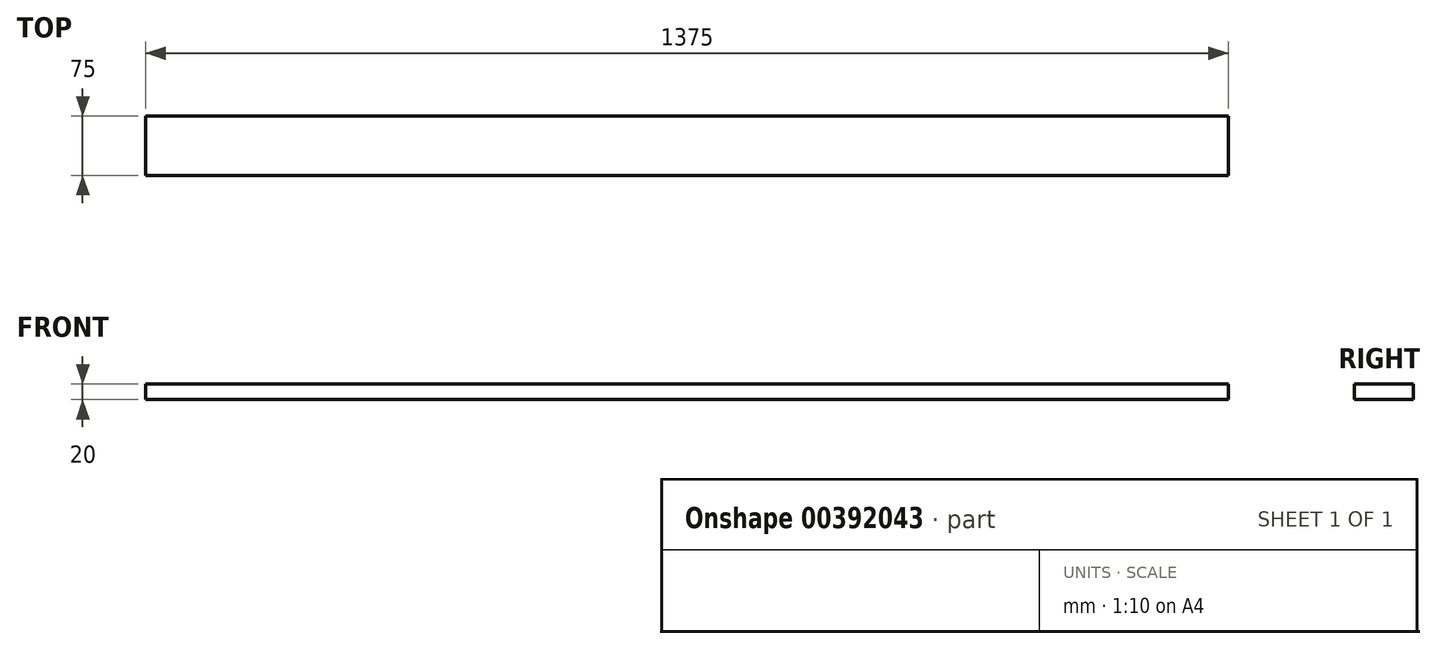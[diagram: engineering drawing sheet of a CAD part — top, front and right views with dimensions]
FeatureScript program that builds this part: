
annotation { "Feature Type Name" : "Feature", "Feature Type Description" : "" }
export const myFeature = defineFeature(function(context is Context, id is Id, definition is map)
    precondition{}
    {
        {
            var Q0;
            Q0=qCreatedBy(makeId("Right.planeOp"),FACE);
            var sketch = newSketch(context, id + "F0", { "sketchPlane" : qUnion([Q0])});
            skLineSegment(sketch, "E0.bottom", {"start": v(37.5, 10) * mm, "end": v(-37.5, 10) * mm});
            skLineSegment(sketch, "E0.top", {"start": v(37.5, -10) * mm, "end": v(-37.5, -10) * mm});
            skLineSegment(sketch, "E0.left", {"start": v(37.5, 10) * mm, "end": v(37.5, -10) * mm});
            skLineSegment(sketch, "E0.right", {"start": v(-37.5, 10) * mm, "end": v(-37.5, -10) * mm});
            skPoint(sketch, "E0.middle", {"position": v(0, 0) * mm});
            skSolve(sketch);
        }
        {
            var Q0;
            Q0 = qSketchRegion(id + "F0", true);
            extrude(context, id + "F1", {"entities" : qUnion([Q0]), "endBound" : BoundingType.SYMMETRIC, "depth" : 1375 * mm});
        }
    });
